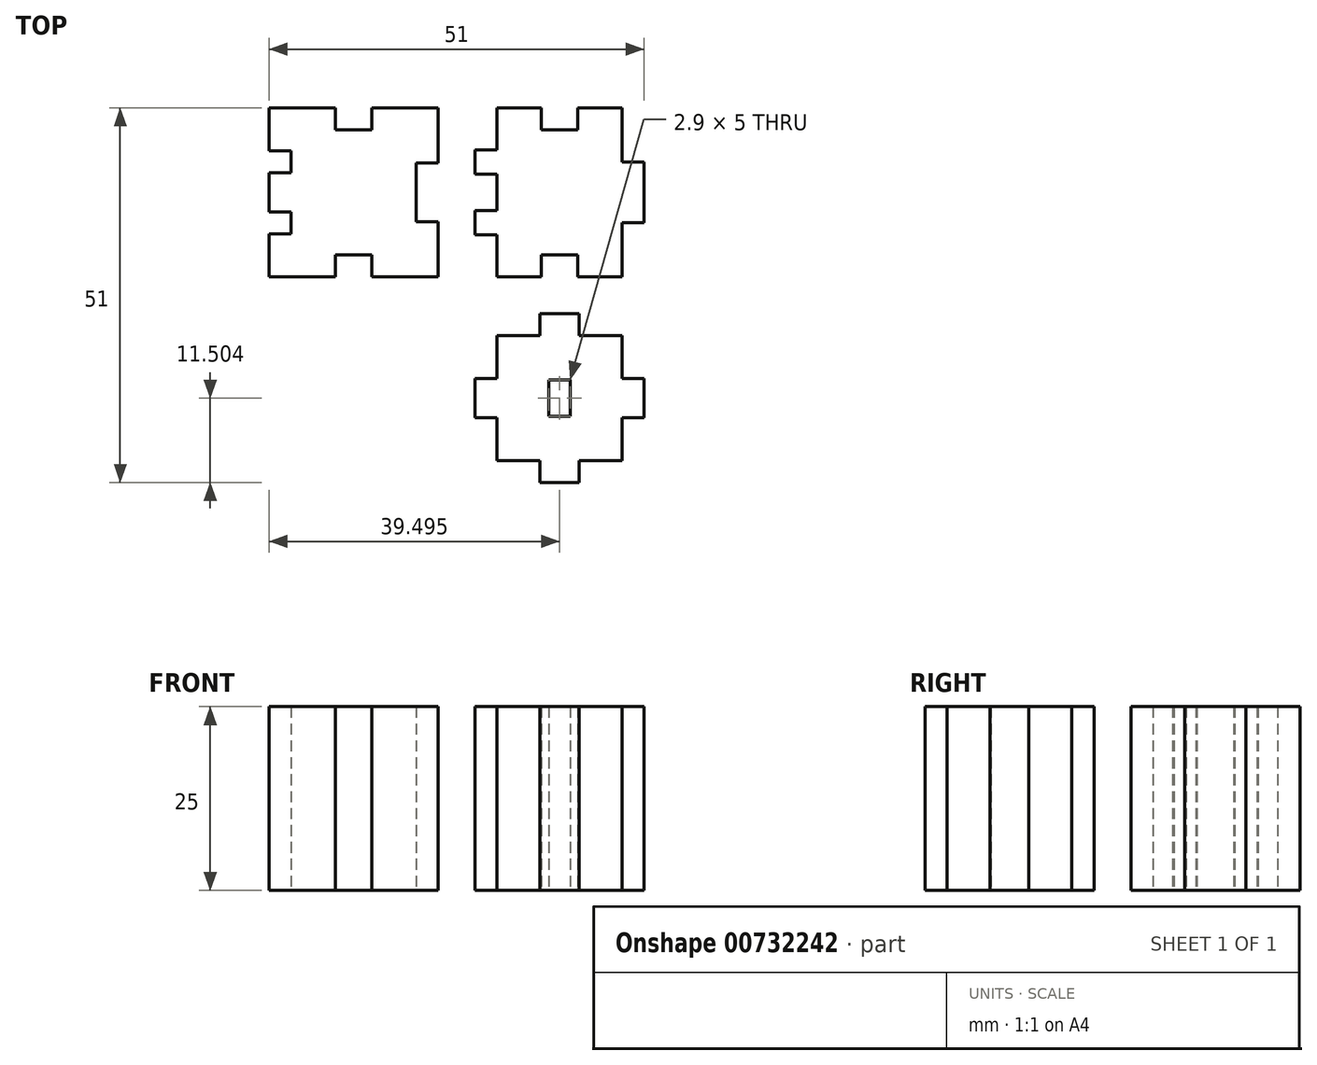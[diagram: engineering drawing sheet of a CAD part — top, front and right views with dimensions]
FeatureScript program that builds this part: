
annotation { "Feature Type Name" : "Feature", "Feature Type Description" : "" }
export const myFeature = defineFeature(function(context is Context, id is Id, definition is map)
    precondition{}
    {
        {
            var Q0;
            Q0=qCreatedBy(makeId("Top.planeOp"),FACE);
            var sketch = newSketch(context, id + "F0", { "sketchPlane" : qUnion([Q0])});
            skLineSegment(sketch, "E0", {"start": v(-29.92, 32.3) * mm, "end": v(-29.92, 26.45) * mm});
            skLineSegment(sketch, "E1", {"start": v(-29.92, 26.45) * mm, "end": v(-26.92, 26.45) * mm});
            skLineSegment(sketch, "E2", {"start": v(-26.92, 26.45) * mm, "end": v(-26.92, 23.45) * mm});
            skLineSegment(sketch, "E3", {"start": v(-26.92, 23.45) * mm, "end": v(-29.92, 23.45) * mm});
            skLineSegment(sketch, "E4", {"start": v(-29.92, 23.45) * mm, "end": v(-29.92, 18.15) * mm});
            skLineSegment(sketch, "E5", {"start": v(-29.92, 18.15) * mm, "end": v(-26.92, 18.15) * mm});
            skLineSegment(sketch, "E6", {"start": v(-26.92, 18.15) * mm, "end": v(-26.92, 15.15) * mm});
            skLineSegment(sketch, "E7", {"start": v(-26.92, 15.15) * mm, "end": v(-29.92, 15.15) * mm});
            skLineSegment(sketch, "E8", {"start": v(-29.92, 15.15) * mm, "end": v(-29.92, 9.3) * mm});
            skLineSegment(sketch, "E9", {"start": v(-6.92, 9.3) * mm, "end": v(-6.92, 16.8) * mm});
            skLineSegment(sketch, "E10", {"start": v(-6.92, 16.8) * mm, "end": v(-9.92, 16.8) * mm});
            skLineSegment(sketch, "E11", {"start": v(-9.92, 16.8) * mm, "end": v(-9.92, 24.8) * mm});
            skLineSegment(sketch, "E12", {"start": v(-9.92, 24.8) * mm, "end": v(-6.92, 24.8) * mm});
            skLineSegment(sketch, "E13", {"start": v(-6.92, 24.8) * mm, "end": v(-6.92, 32.3) * mm});
            skLineSegment(sketch, "E14", {"start": v(-20.92, 32.3) * mm, "end": v(-20.92, 29.3) * mm});
            skLineSegment(sketch, "E15", {"start": v(-20.92, 29.3) * mm, "end": v(-15.92, 29.3) * mm});
            skLineSegment(sketch, "E16", {"start": v(-15.92, 29.3) * mm, "end": v(-15.92, 32.3) * mm});
            skLineSegment(sketch, "E17", {"start": v(-29.92, 32.3) * mm, "end": v(-20.92, 32.3) * mm});
            skLineSegment(sketch, "E18", {"start": v(-15.92, 32.3) * mm, "end": v(-6.92, 32.3) * mm});
            skLineSegment(sketch, "E19", {"start": v(-20.92, 9.3) * mm, "end": v(-20.92, 12.3) * mm});
            skLineSegment(sketch, "E20", {"start": v(-20.92, 12.3) * mm, "end": v(-15.92, 12.3) * mm});
            skLineSegment(sketch, "E21", {"start": v(-15.92, 12.3) * mm, "end": v(-15.92, 9.3) * mm});
            skLineSegment(sketch, "E22", {"start": v(-29.92, 9.3) * mm, "end": v(-20.92, 9.3) * mm});
            skLineSegment(sketch, "E23", {"start": v(-15.92, 9.3) * mm, "end": v(-6.92, 9.3) * mm});
            skPoint(sketch, "E24.endSnap0", {"position": v(-18.42, 12.3) * mm});
            skLineSegment(sketch, "E25", {"start": v(1.08, 32.3) * mm, "end": v(1.08, 26.6) * mm});
            skLineSegment(sketch, "E26", {"start": v(1.08, 26.6) * mm, "end": v(-1.92, 26.6) * mm});
            skLineSegment(sketch, "E27", {"start": v(-1.92, 26.6) * mm, "end": v(-1.92, 23.3) * mm});
            skLineSegment(sketch, "E28", {"start": v(-1.92, 23.3) * mm, "end": v(1.08, 23.3) * mm});
            skLineSegment(sketch, "E29", {"start": v(1.08, 23.3) * mm, "end": v(1.08, 18.3) * mm});
            skLineSegment(sketch, "E30", {"start": v(1.08, 18.3) * mm, "end": v(-1.92, 18.3) * mm});
            skLineSegment(sketch, "E31", {"start": v(-1.92, 18.3) * mm, "end": v(-1.92, 15) * mm});
            skLineSegment(sketch, "E32", {"start": v(-1.92, 15) * mm, "end": v(1.08, 15) * mm});
            skLineSegment(sketch, "E33", {"start": v(1.08, 15) * mm, "end": v(1.08, 9.3) * mm});
            skLineSegment(sketch, "E34", {"start": v(1.08, 9.3) * mm, "end": v(7.08, 9.3) * mm});
            skLineSegment(sketch, "E35", {"start": v(7.08, 9.3) * mm, "end": v(7.08, 12.3) * mm});
            skLineSegment(sketch, "E36", {"start": v(7.08, 12.3) * mm, "end": v(12.08, 12.3) * mm});
            skLineSegment(sketch, "E37", {"start": v(12.08, 12.3) * mm, "end": v(12.08, 9.3) * mm});
            skLineSegment(sketch, "E38", {"start": v(12.08, 9.3) * mm, "end": v(18.08, 9.3) * mm});
            skLineSegment(sketch, "E39", {"start": v(18.08, 9.3) * mm, "end": v(18.08, 16.65) * mm});
            skLineSegment(sketch, "E40", {"start": v(18.08, 16.65) * mm, "end": v(21.08, 16.65) * mm});
            skLineSegment(sketch, "E41", {"start": v(21.08, 16.65) * mm, "end": v(21.08, 24.95) * mm});
            skLineSegment(sketch, "E42", {"start": v(21.08, 24.95) * mm, "end": v(18.08, 24.95) * mm});
            skLineSegment(sketch, "E43", {"start": v(18.08, 24.95) * mm, "end": v(18.08, 32.3) * mm});
            skLineSegment(sketch, "E44", {"start": v(18.08, 32.3) * mm, "end": v(12.08, 32.3) * mm});
            skLineSegment(sketch, "E45", {"start": v(12.08, 32.3) * mm, "end": v(12.08, 29.3) * mm});
            skLineSegment(sketch, "E46", {"start": v(12.08, 29.3) * mm, "end": v(7.08, 29.3) * mm});
            skLineSegment(sketch, "E47", {"start": v(7.08, 29.3) * mm, "end": v(7.08, 32.3) * mm});
            skLineSegment(sketch, "E48", {"start": v(7.08, 32.3) * mm, "end": v(1.08, 32.3) * mm});
            skLineSegment(sketch, "E49", {"start": v(1.08, 1.3) * mm, "end": v(6.93, 1.3) * mm});
            skLineSegment(sketch, "E50", {"start": v(6.93, 1.3) * mm, "end": v(6.93, 4.3) * mm});
            skLineSegment(sketch, "E51", {"start": v(6.93, 4.3) * mm, "end": v(12.23, 4.3) * mm});
            skLineSegment(sketch, "E52", {"start": v(12.23, 4.3) * mm, "end": v(12.23, 1.3) * mm});
            skLineSegment(sketch, "E53", {"start": v(12.23, 1.3) * mm, "end": v(18.08, 1.3) * mm});
            skLineSegment(sketch, "E54", {"start": v(18.08, 1.3) * mm, "end": v(18.08, -4.55) * mm});
            skLineSegment(sketch, "E55", {"start": v(18.08, -4.55) * mm, "end": v(21.08, -4.55) * mm});
            skLineSegment(sketch, "E56", {"start": v(21.08, -4.55) * mm, "end": v(21.08, -9.85) * mm});
            skLineSegment(sketch, "E57", {"start": v(21.08, -9.85) * mm, "end": v(18.08, -9.85) * mm});
            skLineSegment(sketch, "E58", {"start": v(18.08, -9.85) * mm, "end": v(18.08, -15.7) * mm});
            skLineSegment(sketch, "E59", {"start": v(18.08, -15.7) * mm, "end": v(12.23, -15.7) * mm});
            skLineSegment(sketch, "E60", {"start": v(12.23, -15.7) * mm, "end": v(12.23, -18.7) * mm});
            skLineSegment(sketch, "E61", {"start": v(12.23, -18.7) * mm, "end": v(6.93, -18.7) * mm});
            skLineSegment(sketch, "E62", {"start": v(6.93, -18.7) * mm, "end": v(6.93, -15.7) * mm});
            skLineSegment(sketch, "E63", {"start": v(6.93, -15.7) * mm, "end": v(1.08, -15.7) * mm});
            skLineSegment(sketch, "E64", {"start": v(1.08, -15.7) * mm, "end": v(1.08, -9.85) * mm});
            skLineSegment(sketch, "E65", {"start": v(1.08, -9.85) * mm, "end": v(-1.92, -9.85) * mm});
            skLineSegment(sketch, "E66", {"start": v(-1.92, -9.85) * mm, "end": v(-1.92, -4.55) * mm});
            skLineSegment(sketch, "E67", {"start": v(-1.92, -4.55) * mm, "end": v(1.08, -4.55) * mm});
            skLineSegment(sketch, "E68", {"start": v(1.08, -4.55) * mm, "end": v(1.08, 1.3) * mm});
            skLineSegment(sketch, "E69.bottom", {"start": v(8.13, -4.7) * mm, "end": v(11.03, -4.7) * mm});
            skLineSegment(sketch, "E69.top", {"start": v(8.13, -9.7) * mm, "end": v(11.03, -9.7) * mm});
            skLineSegment(sketch, "E69.left", {"start": v(8.13, -4.7) * mm, "end": v(8.13, -9.7) * mm});
            skLineSegment(sketch, "E69.right", {"start": v(11.03, -4.7) * mm, "end": v(11.03, -9.7) * mm});
            skPoint(sketch, "E70", {"position": v(9.58, -4.7) * mm});
            skPoint(sketch, "E71", {"position": v(9.58, 4.3) * mm});
            skPoint(sketch, "E72", {"position": v(11.03, -7.2) * mm});
            skPoint(sketch, "E73", {"position": v(21.08, -7.2) * mm});
            skSolve(sketch);
        }
        {
            var Q0;
            Q0=makeQuery(id+"F0.imprint","IMPRINT",FACE,{"disambiguationData":[TD([[makeQuery(id+"F0.imprint","IMPRINT",EDGE,{"derivedFrom":sQuery(id+"F0.wireOp",EDGE,"E0")}),1.0]])]});
            var Q1;
            Q1=makeQuery(id+"F0.imprint","IMPRINT",FACE,{"disambiguationData":[TD([[makeQuery(id+"F0.imprint","IMPRINT",EDGE,{"derivedFrom":sQuery(id+"F0.wireOp",EDGE,"E25")}),1.0]])]});
            var Q2;
            Q2=makeQuery(id+"F0.imprint","IMPRINT",FACE,{"disambiguationData":[TD([[makeQuery(id+"F0.imprint","IMPRINT",EDGE,{"derivedFrom":sQuery(id+"F0.wireOp",EDGE,"E49")}),-1.0]])]});
            extrude(context, id + "F1", {"entities" : qUnion([Q0, Q1, Q2]), "depth" : 25 * mm, "offsetDistance" : 25 * mm});
        }
    });
